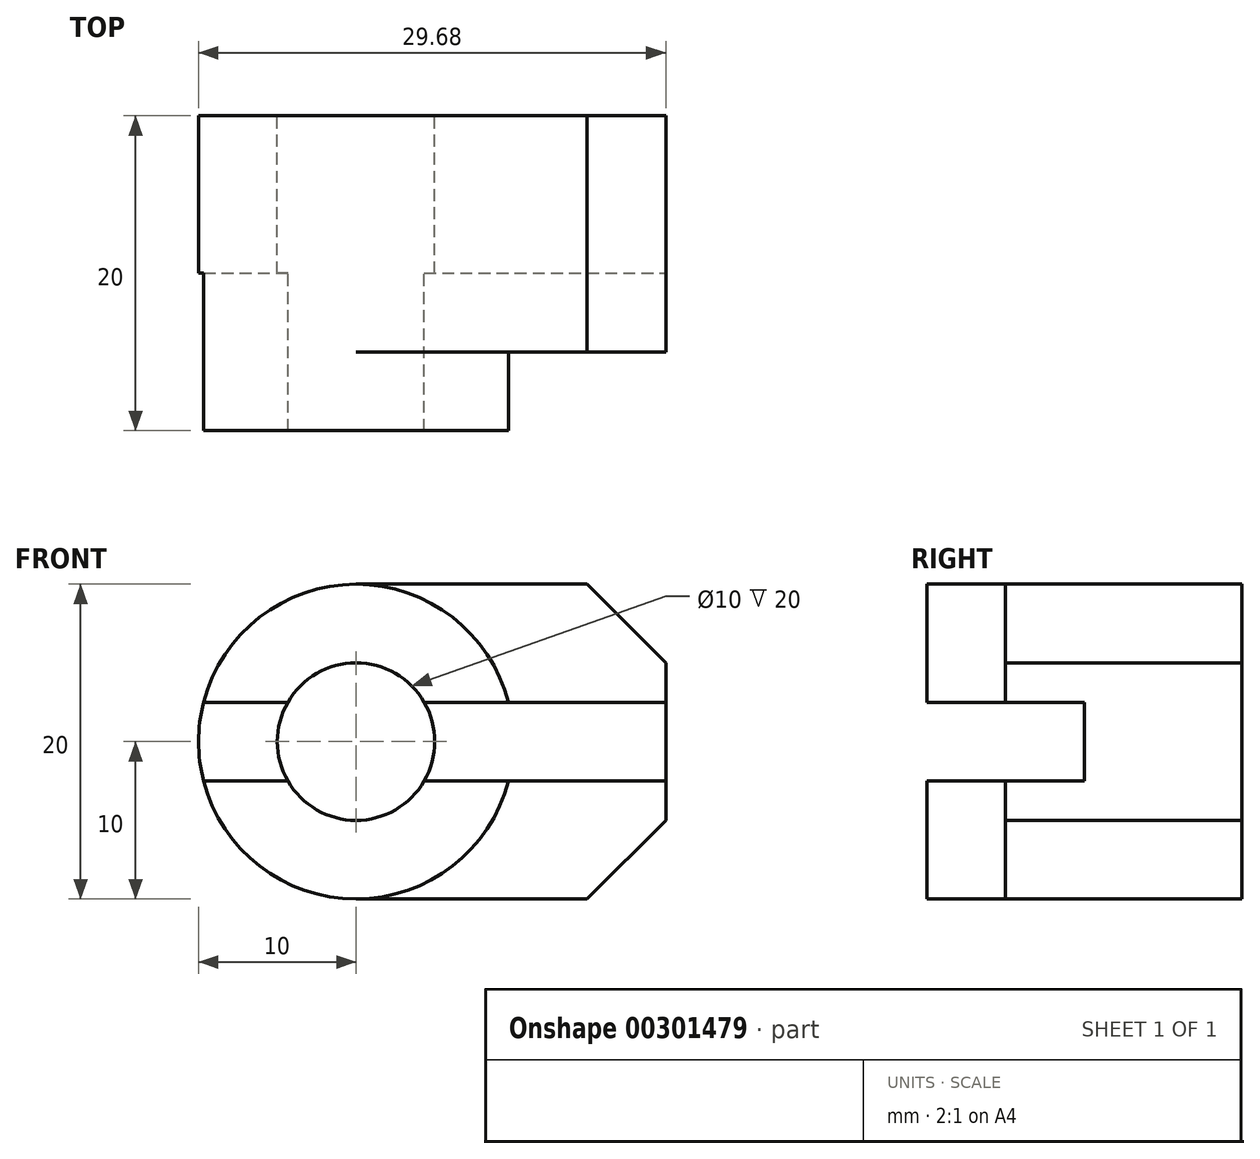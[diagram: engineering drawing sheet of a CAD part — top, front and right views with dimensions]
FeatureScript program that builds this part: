
annotation { "Feature Type Name" : "Feature", "Feature Type Description" : "" }
export const myFeature = defineFeature(function(context is Context, id is Id, definition is map)
    precondition{}
    {
        {
            var Q0;
            Q0=qCreatedBy(makeId("Front.planeOp"),FACE);
            var sketch = newSketch(context, id + "F0", { "sketchPlane" : qUnion([Q0])});
            skCircle(sketch, "E0", {"center": v(0, 0) * mm, "radius": 5 * mm});
            skArc(sketch, "E1", {"start": v(9.68, 2.5) * mm, "mid": v(-10, 0) * mm, "end": v(9.68, -2.5) * mm});
            skLineSegment(sketch, "E2", {"start": v(0, 10) * mm, "end": v(14.68, 10) * mm});
            skLineSegment(sketch, "E3", {"start": v(14.68, 10) * mm, "end": v(19.68, 5) * mm});
            skLineSegment(sketch, "E4", {"start": v(19.68, 5) * mm, "end": v(19.68, -5) * mm});
            skLineSegment(sketch, "E5", {"start": v(19.68, -5) * mm, "end": v(14.68, -10) * mm});
            skLineSegment(sketch, "E6", {"start": v(14.68, -10) * mm, "end": v(0, -10) * mm});
            skLineSegment(sketch, "E7", {"start": v(-9.68, 2.5) * mm, "end": v(-4.33, 2.5) * mm});
            skLineSegment(sketch, "E8", {"start": v(-9.68, -2.5) * mm, "end": v(-4.33, -2.5) * mm});
            skLineSegment(sketch, "E9.trimOffspring", {"start": v(4.33, 2.5) * mm, "end": v(19.68, 2.5) * mm});
            skLineSegment(sketch, "E10.trimOffspring", {"start": v(4.33, -2.5) * mm, "end": v(19.68, -2.5) * mm});
            skSolve(sketch);
        }
        {
            var Q0;
            {var subQ0=sQuery(id+"F0.wireOp",EDGE,"E7");Q0=makeQuery(id+"F0.imprint","IMPRINT",FACE,{"disambiguationData":[TD([[makeQuery(id+"F0.imprint","IMPRINT",EDGE,{"derivedFrom":subQ0}),1.0]])]});}
            var Q1;
            {var subQ4=sQuery(id+"F0.wireOp",EDGE,"E8");Q1=makeQuery(id+"F0.imprint","IMPRINT",FACE,{"disambiguationData":[TD([[makeQuery(id+"F0.imprint","IMPRINT",EDGE,{"derivedFrom":subQ4}),-1.0]])]});}
            extrude(context, id + "F1", {"entities" : qUnion([Q0, Q1]), "depth" : 20 * mm});
        }
        {
            var Q0;
            {var subQ4=sQuery(id+"F0.wireOp",EDGE,"E2");Q0=makeQuery(id+"F0.imprint","IMPRINT",FACE,{"disambiguationData":[TD([[makeQuery(id+"F0.imprint","IMPRINT",EDGE,{"derivedFrom":subQ4}),-1.0]])]});}
            var Q1;
            {var subQ1=sQuery(id+"F0.wireOp",EDGE,"E5");Q1=makeQuery(id+"F0.imprint","IMPRINT",FACE,{"disambiguationData":[TD([[makeQuery(id+"F0.imprint","IMPRINT",EDGE,{"derivedFrom":subQ1}),-1.0]])]});}
            extrude(context, id + "F2", {"entities" : qUnion([Q0, Q1]), "operationType" : NewBodyOperationType.ADD, "depth" : 15 * mm});
        }
        {
            var Q0;
            {var subQ0=sQuery(id+"F0.wireOp",EDGE,"E9.trimOffspring");var subQ7=sQuery(id+"F0.wireOp",EDGE,"E0");var subQ8=makeQuery(id+"F0.imprint","INTERSECT",VERTEX,{"derivedFrom":[subQ7,subQ0]});Q0=makeQuery(id+"F0.imprint","IMPRINT",FACE,{"disambiguationData":[TD([[makeQuery(id+"F0.imprint","IMPRINT",EDGE,{"disambiguationData":[TD([[subQ8,1.0]])],"derivedFrom":subQ7}),-1.0]])]});}
            var Q1;
            {var subQ0=sQuery(id+"F0.wireOp",EDGE,"E7");Q1=makeQuery(id+"F0.imprint","IMPRINT",FACE,{"disambiguationData":[TD([[makeQuery(id+"F0.imprint","IMPRINT",EDGE,{"derivedFrom":subQ0}),-1.0]])]});}
            extrude(context, id + "F3", {"entities" : qUnion([Q0, Q1]), "operationType" : NewBodyOperationType.ADD, "depth" : 10 * mm});
        }
    });
